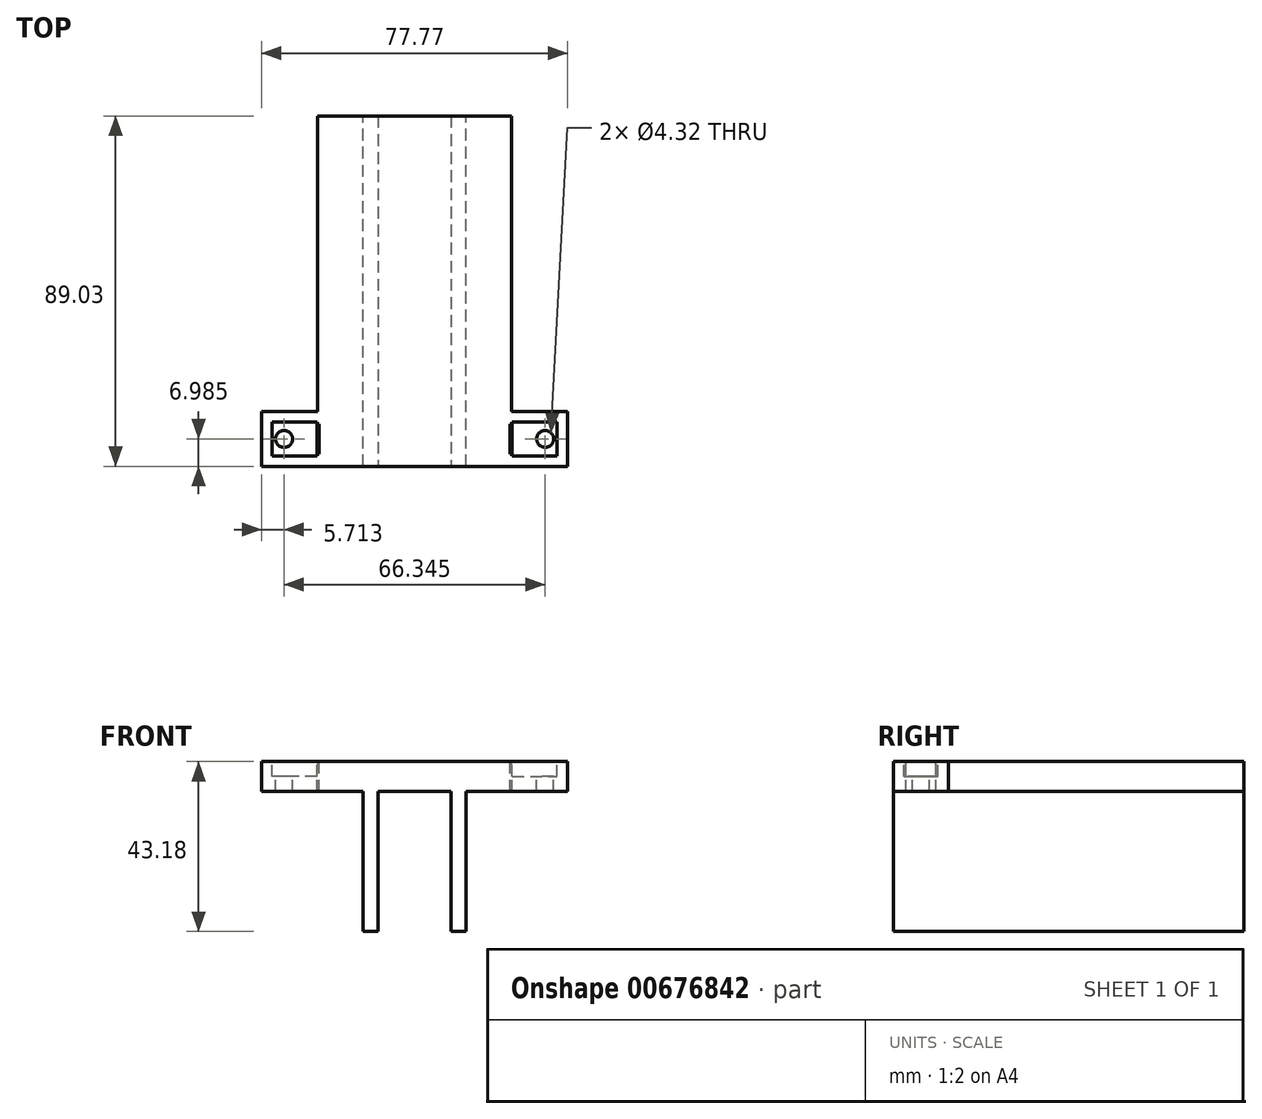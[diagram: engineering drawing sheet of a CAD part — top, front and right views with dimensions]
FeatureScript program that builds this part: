
annotation { "Feature Type Name" : "Feature", "Feature Type Description" : "" }
export const myFeature = defineFeature(function(context is Context, id is Id, definition is map)
    precondition{}
    {
        {
            var Q0;
            Q0=qCreatedBy(makeId("Top.planeOp"),FACE);
            var sketch = newSketch(context, id + "F0", { "sketchPlane" : qUnion([Q0])});
            skLineSegment(sketch, "E0.bottom", {"start": v(0, 0) * mm, "end": v(31.75, 0) * mm});
            skLineSegment(sketch, "E0.top", {"start": v(0, -63.5) * mm, "end": v(31.75, -63.5) * mm});
            skLineSegment(sketch, "E0.left", {"start": v(0, 0) * mm, "end": v(0, -63.5) * mm});
            skLineSegment(sketch, "E0.right", {"start": v(31.75, 0) * mm, "end": v(31.75, -63.5) * mm});
            skSolve(sketch);
        }
        {
            var Q0;
            Q0=qSketchRegion(id+"F0",true);
            extrude(context, id + "F1", {"entities" : qUnion([Q0]), "depth" : 7.62 * mm, "offsetDistance" : 25.4 * mm});
        }
        {
            var Q0;
            Q0=makeQuery(id+"F1.opExtrude","SWEPT_FACE",FACE,{"disambiguationData":[OSD([sQuery(id+"F0.wireOp",EDGE,"E0.top")])]});
            var sketch = newSketch(context, id + "F2", { "sketchPlane" : qUnion([Q0])});
            skLineSegment(sketch, "E1.bottom", {"start": v(21.74, 0) * mm, "end": v(10, 0) * mm});
            skLineSegment(sketch, "E1.top", {"start": v(21.74, 7.62) * mm, "end": v(10, 7.62) * mm});
            skLineSegment(sketch, "E1.left", {"start": v(21.74, 0) * mm, "end": v(21.74, 7.62) * mm});
            skLineSegment(sketch, "E1.right", {"start": v(10, 0) * mm, "end": v(10, 7.62) * mm});
            skSolve(sketch);
        }
        {
            var Q0;
            Q0=qSketchRegion(id+"F2",true);
            extrude(context, id + "F3", {"entities" : qUnion([Q0]), "operationType" : NewBodyOperationType.ADD, "depth" : 19.05 * mm, "offsetDistance" : 25.4 * mm});
        }
        {
            var Q0;
            Q0=makeQuery(id+"F3.opExtrude","SWEPT_FACE",FACE,{"disambiguationData":[OSD([sQuery(id+"F2.wireOp",EDGE,"E1.right")])]});
            var sketch = newSketch(context, id + "F4", { "sketchPlane" : qUnion([Q0])});
            skLineSegment(sketch, "E2.bottom", {"start": v(82.55, 7.62) * mm, "end": v(68.58, 7.62) * mm});
            skLineSegment(sketch, "E2.top", {"start": v(82.55, 0) * mm, "end": v(68.58, 0) * mm});
            skLineSegment(sketch, "E2.left", {"start": v(82.55, 7.62) * mm, "end": v(82.55, 0) * mm});
            skLineSegment(sketch, "E2.right", {"start": v(68.58, 7.62) * mm, "end": v(68.58, 0) * mm});
            skSolve(sketch);
        }
        {
            var Q0;
            Q0=makeQuery(id+"F4.imprint","IMPRINT",FACE,{"disambiguationData":[TD([[makeQuery(id+"F4.imprint","IMPRINT",EDGE,{"derivedFrom":sQuery(id+"F4.wireOp",EDGE,"E2.bottom")}),1.0]])]});
            extrude(context, id + "F5", {"entities" : qUnion([Q0]), "operationType" : NewBodyOperationType.ADD, "depth" : 33.02 * mm, "offsetDistance" : 25.4 * mm});
        }
        {
            var Q0;
            Q0=makeQuery(id+"F3.opExtrude","SWEPT_FACE",FACE,{"disambiguationData":[OSD([sQuery(id+"F2.wireOp",EDGE,"E1.left")])]});
            var sketch = newSketch(context, id + "F6", { "sketchPlane" : qUnion([Q0])});
            skLineSegment(sketch, "E3.bottom", {"start": v(-82.55, 0) * mm, "end": v(-68.58, 0) * mm});
            skLineSegment(sketch, "E3.top", {"start": v(-82.55, 7.62) * mm, "end": v(-68.58, 7.62) * mm});
            skLineSegment(sketch, "E3.left", {"start": v(-82.55, 0) * mm, "end": v(-82.55, 7.62) * mm});
            skLineSegment(sketch, "E3.right", {"start": v(-68.58, 0) * mm, "end": v(-68.58, 7.62) * mm});
            skSolve(sketch);
        }
        {
            var Q0;
            Q0=makeQuery(id+"F6.imprint","IMPRINT",FACE,{"disambiguationData":[TD([[makeQuery(id+"F6.imprint","IMPRINT",EDGE,{"derivedFrom":sQuery(id+"F6.wireOp",EDGE,"E3.bottom")}),1.0]])]});
            extrude(context, id + "F7", {"entities" : qUnion([Q0]), "operationType" : NewBodyOperationType.ADD, "depth" : 33.02 * mm, "offsetDistance" : 25.4 * mm});
        }
        {
            var Q0;
            Q0=makeQuery(id+"F7.boolean.opBoolean","MERGE",FACE,{"derivedFrom":[makeQuery(id+"F5.boolean.opBoolean","MERGE",FACE,{"derivedFrom":[makeQuery(id+"F3.boolean.opBoolean","MERGE",FACE,{"derivedFrom":[makeQuery(id+"F1.opExtrude","CAP_FACE",FACE,{"disambiguationData":[OSD([sQuery(id+"F0.wireOp",EDGE,"E0.bottom"),sQuery(id+"F0.wireOp",EDGE,"E0.top"),sQuery(id+"F0.wireOp",EDGE,"E0.left"),sQuery(id+"F0.wireOp",EDGE,"E0.right"),sQuery(id+"F0.wireOp",EDGE,"ZbQCodWJ-8rFa-9hVk-pMdy-9ETOQNlD702V"),sQuery(id+"F0.wireOp",EDGE,"mox7wiXO-owZT-BLzV-svZ2-wi7KJzRx0I65")])],"isStart":false}),makeQuery(id+"F3.opExtrude","SWEPT_FACE",FACE,{"disambiguationData":[OSD([sQuery(id+"F2.wireOp",EDGE,"E1.top")])]})]}),makeQuery(id+"F5.opExtrude","SWEPT_FACE",FACE,{"disambiguationData":[OSD([sQuery(id+"F4.wireOp",EDGE,"E2.bottom")])]})]}),makeQuery(id+"F7.opExtrude","SWEPT_FACE",FACE,{"disambiguationData":[OSD([sQuery(id+"F6.wireOp",EDGE,"E3.top")])]})]});
            var sketch = newSketch(context, id + "F8", { "sketchPlane" : qUnion([Q0])});
            skLineSegment(sketch, "E4.bottom", {"start": v(51.59, -71.75) * mm, "end": v(37.62, -71.75) * mm});
            skLineSegment(sketch, "E4.top", {"start": v(51.59, -79.37) * mm, "end": v(37.62, -79.37) * mm});
            skLineSegment(sketch, "E4.left", {"start": v(51.59, -71.75) * mm, "end": v(51.59, -79.37) * mm});
            skLineSegment(sketch, "E4.right", {"start": v(37.62, -71.75) * mm, "end": v(37.62, -79.37) * mm});
            skLineSegment(sketch, "E5.bottom", {"start": v(-5.87, -71.75) * mm, "end": v(-19.84, -71.75) * mm});
            skLineSegment(sketch, "E5.top", {"start": v(-5.87, -79.37) * mm, "end": v(-19.84, -79.37) * mm});
            skLineSegment(sketch, "E5.left", {"start": v(-5.87, -71.75) * mm, "end": v(-5.87, -79.37) * mm});
            skLineSegment(sketch, "E5.right", {"start": v(-19.84, -71.75) * mm, "end": v(-19.84, -79.37) * mm});
            skCircle(sketch, "E6", {"center": v(49.05, -75.56) * mm, "radius": 2.16 * mm});
            skCircle(sketch, "E7", {"center": v(-17.3, -75.56) * mm, "radius": 2.16 * mm});
            skLineSegment(sketch, "E8.bottom", {"start": v(37.62, -71.75) * mm, "end": v(40.16, -71.75) * mm});
            skLineSegment(sketch, "E8.top", {"start": v(37.62, -79.37) * mm, "end": v(40.16, -79.37) * mm});
            skLineSegment(sketch, "E8.right", {"start": v(40.16, -71.75) * mm, "end": v(40.16, -79.37) * mm});
            skLineSegment(sketch, "E9.bottom", {"start": v(-5.87, -71.75) * mm, "end": v(-8.4, -71.75) * mm});
            skLineSegment(sketch, "E9.top", {"start": v(-5.87, -79.37) * mm, "end": v(-8.4, -79.37) * mm});
            skLineSegment(sketch, "E9.right", {"start": v(-8.4, -71.75) * mm, "end": v(-8.4, -79.37) * mm});
            skLineSegment(sketch, "E10.bottom", {"start": v(40.67, -79.88) * mm, "end": v(37.1, -79.88) * mm});
            skLineSegment(sketch, "E10.top", {"start": v(40.67, -71.25) * mm, "end": v(37.1, -71.25) * mm});
            skLineSegment(sketch, "E10.left", {"start": v(40.67, -79.88) * mm, "end": v(40.67, -71.25) * mm});
            skLineSegment(sketch, "E10.right", {"start": v(37.1, -79.88) * mm, "end": v(37.1, -71.25) * mm});
            skLineSegment(sketch, "E11.bottom", {"start": v(-5.36, -79.88) * mm, "end": v(-8.92, -79.88) * mm});
            skLineSegment(sketch, "E11.top", {"start": v(-5.36, -71.25) * mm, "end": v(-8.92, -71.25) * mm});
            skLineSegment(sketch, "E11.left", {"start": v(-5.36, -79.88) * mm, "end": v(-5.36, -71.25) * mm});
            skLineSegment(sketch, "E11.right", {"start": v(-8.92, -79.88) * mm, "end": v(-8.92, -71.25) * mm});
            skLineSegment(sketch, "E12.left", {"start": v(40.67, -71.25) * mm, "end": v(40.67, -79.37) * mm});
            skLineSegment(sketch, "E13.bottom", {"start": v(40.67, -71.25) * mm, "end": v(52.1, -71.25) * mm});
            skLineSegment(sketch, "E13.top", {"start": v(40.67, -79.88) * mm, "end": v(52.1, -79.88) * mm});
            skLineSegment(sketch, "E13.left", {"start": v(40.67, -71.25) * mm, "end": v(40.67, -79.88) * mm});
            skLineSegment(sketch, "E13.right", {"start": v(52.1, -71.25) * mm, "end": v(52.1, -79.88) * mm});
            skLineSegment(sketch, "E14.bottom", {"start": v(-8.92, -71.25) * mm, "end": v(-20.35, -71.25) * mm});
            skLineSegment(sketch, "E14.top", {"start": v(-8.92, -79.88) * mm, "end": v(-20.35, -79.88) * mm});
            skLineSegment(sketch, "E14.left", {"start": v(-8.92, -71.25) * mm, "end": v(-8.92, -79.88) * mm});
            skLineSegment(sketch, "E14.right", {"start": v(-20.35, -71.25) * mm, "end": v(-20.35, -79.88) * mm});
            skSolve(sketch);
        }
        {
            var Q0;
            Q0=makeQuery(id+"F8.imprint","IMPRINT",FACE,{"disambiguationData":[TD([[makeQuery(id+"F8.imprint","IMPRINT",EDGE,{"derivedFrom":sQuery(id+"F8.wireOp",EDGE,"E6")}),1.0]])]});
            var Q1;
            {var subQ0=sQuery(id+"F8.wireOp",EDGE,"E8.bottom");Q1=makeQuery(id+"F8.imprint","IMPRINT",FACE,{"disambiguationData":[TD([[makeQuery(id+"F8.imprint","IMPRINT",EDGE,{"derivedFrom":subQ0}),1.0]])]});}
            var Q2;
            {var subQ0=sQuery(id+"F8.wireOp",EDGE,"E8.right");Q2=makeQuery(id+"F8.imprint","IMPRINT",FACE,{"disambiguationData":[TD([[makeQuery(id+"F8.imprint","IMPRINT",EDGE,{"derivedFrom":subQ0}),1.0]])]});}
            var Q3;
            Q3=makeQuery(id+"F8.imprint","IMPRINT",FACE,{"disambiguationData":[TD([[makeQuery(id+"F8.imprint","IMPRINT",EDGE,{"derivedFrom":sQuery(id+"F8.wireOp",EDGE,"E8.bottom")}),-1.0]])]});
            var Q4;
            Q4=makeQuery(id+"F8.imprint","IMPRINT",FACE,{"disambiguationData":[TD([[makeQuery(id+"F8.imprint","IMPRINT",EDGE,{"derivedFrom":sQuery(id+"F8.wireOp",EDGE,"E7")}),1.0]])]});
            var Q5;
            {var subQ0=sQuery(id+"F8.wireOp",EDGE,"E9.bottom");Q5=makeQuery(id+"F8.imprint","IMPRINT",FACE,{"disambiguationData":[TD([[makeQuery(id+"F8.imprint","IMPRINT",EDGE,{"derivedFrom":subQ0}),-1.0]])]});}
            var Q6;
            {var subQ0=sQuery(id+"F8.wireOp",EDGE,"E9.right");Q6=makeQuery(id+"F8.imprint","IMPRINT",FACE,{"disambiguationData":[TD([[makeQuery(id+"F8.imprint","IMPRINT",EDGE,{"derivedFrom":subQ0}),-1.0]])]});}
            var Q7;
            Q7=makeQuery(id+"F8.imprint","IMPRINT",FACE,{"disambiguationData":[TD([[makeQuery(id+"F8.imprint","IMPRINT",EDGE,{"derivedFrom":sQuery(id+"F8.wireOp",EDGE,"E9.bottom")}),1.0]])]});
            extrude(context, id + "F9", {"entities" : qUnion([Q0, Q1, Q2, Q3, Q4, Q5, Q6, Q7]), "operationType" : NewBodyOperationType.REMOVE, "endBound" : BoundingType.THROUGH_ALL, "oppositeDirection" : true, "depth" : 25.4 * mm, "offsetDistance" : 25.4 * mm});
        }
        {
            var Q0;
            Q0=makeQuery(id+"F3.opExtrude","SWEPT_FACE",FACE,{"disambiguationData":[OSD([sQuery(id+"F2.wireOp",EDGE,"E1.right")])]});
            extrude(context, id + "F10", {"entities" : qUnion([Q0]), "operationType" : NewBodyOperationType.ADD, "depth" : 10 * mm, "offsetDistance" : 25.4 * mm});
        }
        {
            var Q0;
            Q0=makeQuery(id+"F3.opExtrude","SWEPT_FACE",FACE,{"disambiguationData":[OSD([sQuery(id+"F2.wireOp",EDGE,"E1.left")])]});
            extrude(context, id + "F11", {"entities" : qUnion([Q0]), "operationType" : NewBodyOperationType.ADD, "depth" : 10 * mm, "offsetDistance" : 25.4 * mm});
        }
        {
            var Q0;
            {var subQ0=sQuery(id+"F8.wireOp",EDGE,"E4.left");Q0=makeQuery(id+"F8.imprint","IMPRINT",FACE,{"disambiguationData":[TD([[makeQuery(id+"F8.imprint","IMPRINT",EDGE,{"derivedFrom":subQ0}),-1.0]])]});}
            var Q1;
            {var subQ1=sQuery(id+"F8.wireOp",EDGE,"E4.left");Q1=makeQuery(id+"F8.imprint","IMPRINT",FACE,{"disambiguationData":[TD([[makeQuery(id+"F8.imprint","IMPRINT",EDGE,{"derivedFrom":subQ1}),1.0]])]});}
            var Q2;
            {var subQ0=sQuery(id+"F8.wireOp",EDGE,"E5.right");Q2=makeQuery(id+"F8.imprint","IMPRINT",FACE,{"disambiguationData":[TD([[makeQuery(id+"F8.imprint","IMPRINT",EDGE,{"derivedFrom":subQ0}),1.0]])]});}
            var Q3;
            {var subQ1=sQuery(id+"F8.wireOp",EDGE,"E5.right");Q3=makeQuery(id+"F8.imprint","IMPRINT",FACE,{"disambiguationData":[TD([[makeQuery(id+"F8.imprint","IMPRINT",EDGE,{"derivedFrom":subQ1}),-1.0]])]});}
            extrude(context, id + "F12", {"entities" : qUnion([Q0, Q1, Q2, Q3]), "operationType" : NewBodyOperationType.REMOVE, "oppositeDirection" : true, "depth" : 3.8 * mm, "offsetDistance" : 25.4 * mm});
        }
        {
            var Q0;
            Q0=makeQuery(id+"F10.boolean.opBoolean","MERGE",FACE,{"derivedFrom":[makeQuery(id+"F1.opExtrude","SWEPT_FACE",FACE,{"disambiguationData":[OSD([sQuery(id+"F0.wireOp",EDGE,"E0.left")])]}),makeQuery(id+"F10.opExtrude","CAP_FACE",FACE,{"disambiguationData":[OSD([sQuery(id+"F2.wireOp",EDGE,"E1.right")])],"isStart":false})]});
            extrude(context, id + "F13", {"entities" : qUnion([Q0]), "operationType" : NewBodyOperationType.ADD, "depth" : 8.75 * mm, "offsetDistance" : 25.4 * mm});
        }
        {
            var Q0;
            Q0=makeQuery(id+"F11.boolean.opBoolean","MERGE",FACE,{"derivedFrom":[makeQuery(id+"F1.opExtrude","SWEPT_FACE",FACE,{"disambiguationData":[OSD([sQuery(id+"F0.wireOp",EDGE,"E0.right")])]}),makeQuery(id+"F11.opExtrude","CAP_FACE",FACE,{"disambiguationData":[OSD([sQuery(id+"F2.wireOp",EDGE,"E1.left")])],"isStart":false})]});
            extrude(context, id + "F14", {"entities" : qUnion([Q0]), "operationType" : NewBodyOperationType.ADD, "depth" : 8.75 * mm, "offsetDistance" : 25.4 * mm});
        }
        {
            var Q0;
            {var subQ0=sQuery(id+"F0.wireOp",EDGE,"E0.bottom");Q0=makeQuery(id+"F14.boolean.opBoolean","MERGE",FACE,{"derivedFrom":[makeQuery(id+"F13.boolean.opBoolean","MERGE",FACE,{"derivedFrom":[makeQuery(id+"F1.opExtrude","SWEPT_FACE",FACE,{"disambiguationData":[OSD([subQ0])]}),makeQuery(id+"F13.opExtrude","SWEPT_FACE",FACE,{"disambiguationData":[OSD([subQ0,sQuery(id+"F0.wireOp",EDGE,"E0.left")])]})]}),makeQuery(id+"F14.opExtrude","SWEPT_FACE",FACE,{"disambiguationData":[OSD([subQ0,sQuery(id+"F0.wireOp",EDGE,"E0.right")])]})]});}
            extrude(context, id + "F15", {"entities" : qUnion([Q0]), "operationType" : NewBodyOperationType.ADD, "depth" : 6.48 * mm, "offsetDistance" : 25.4 * mm});
        }
        {
            var Q0;
            {var subQ0=sQuery(id+"F2.wireOp",EDGE,"E1.left");var subQ1=sQuery(id+"F2.wireOp",EDGE,"E1.bottom");var subQ2=sQuery(id+"F0.wireOp",EDGE,"E0.right");var subQ3=sQuery(id+"F0.wireOp",EDGE,"E0.top");var subQ4=sQuery(id+"F2.wireOp",EDGE,"E1.right");var subQ5=sQuery(id+"F0.wireOp",EDGE,"E0.left");Q0=makeQuery(id+"F14.boolean.opBoolean","MERGE",FACE,{"derivedFrom":[makeQuery(id+"F13.boolean.opBoolean","MERGE",FACE,{"derivedFrom":[makeQuery(id+"F11.boolean.opBoolean","MERGE",FACE,{"derivedFrom":[makeQuery(id+"F10.boolean.opBoolean","MERGE",FACE,{"derivedFrom":[makeQuery(id+"F7.boolean.opBoolean","MERGE",FACE,{"derivedFrom":[makeQuery(id+"F5.boolean.opBoolean","MERGE",FACE,{"derivedFrom":[makeQuery(id+"F3.boolean.opBoolean","MERGE",FACE,{"derivedFrom":[makeQuery(id+"F1.opExtrude","CAP_FACE",FACE,{"disambiguationData":[OSD([sQuery(id+"F0.wireOp",EDGE,"E0.bottom"),subQ3,subQ5,subQ2])],"isStart":true}),makeQuery(id+"F3.opExtrude","SWEPT_FACE",FACE,{"disambiguationData":[OSD([subQ1])]})]}),makeQuery(id+"F5.opExtrude","SWEPT_FACE",FACE,{"disambiguationData":[OSD([sQuery(id+"F4.wireOp",EDGE,"E2.top")])]})]}),makeQuery(id+"F7.opExtrude","SWEPT_FACE",FACE,{"disambiguationData":[OSD([sQuery(id+"F6.wireOp",EDGE,"E3.bottom")])]})]}),makeQuery(id+"F10.opExtrude","SWEPT_FACE",FACE,{"disambiguationData":[OSD([subQ3,subQ1,subQ4])]})]}),makeQuery(id+"F11.opExtrude","SWEPT_FACE",FACE,{"disambiguationData":[OSD([subQ3,subQ1,subQ0])]})]}),makeQuery(id+"F13.opExtrude","SWEPT_FACE",FACE,{"disambiguationData":[OSD([subQ3,subQ5,subQ1,subQ4])]})]}),makeQuery(id+"F14.opExtrude","SWEPT_FACE",FACE,{"disambiguationData":[OSD([subQ3,subQ2,subQ1,subQ0])]})]});}
            var sketch = newSketch(context, id + "F16", { "sketchPlane" : qUnion([Q0])});
            skLineSegment(sketch, "E15.bottom", {"start": v(25.13, -6.48) * mm, "end": v(6.62, -6.48) * mm});
            skLineSegment(sketch, "E15.top", {"start": v(25.13, 82.55) * mm, "end": v(6.62, 82.55) * mm});
            skLineSegment(sketch, "E15.left", {"start": v(25.13, -6.48) * mm, "end": v(25.13, 82.55) * mm});
            skLineSegment(sketch, "E15.right", {"start": v(6.62, -6.48) * mm, "end": v(6.62, 82.55) * mm});
            skLineSegment(sketch, "E16.bottom", {"start": v(6.62, -6.48) * mm, "end": v(25.13, -6.48) * mm});
            skLineSegment(sketch, "E16.top", {"start": v(6.62, -1.4) * mm, "end": v(25.13, -1.4) * mm});
            skLineSegment(sketch, "E16.left", {"start": v(6.62, -6.48) * mm, "end": v(6.62, -1.4) * mm});
            skLineSegment(sketch, "E16.right", {"start": v(25.13, -6.48) * mm, "end": v(25.13, -1.4) * mm});
            skLineSegment(sketch, "E17.bottom", {"start": v(6.62, 82.55) * mm, "end": v(25.13, 82.55) * mm});
            skLineSegment(sketch, "E17.top", {"start": v(6.62, 77.47) * mm, "end": v(25.13, 77.47) * mm});
            skLineSegment(sketch, "E17.left", {"start": v(6.62, 82.55) * mm, "end": v(6.62, 77.47) * mm});
            skLineSegment(sketch, "E17.right", {"start": v(25.13, 82.55) * mm, "end": v(25.13, 77.47) * mm});
            skLineSegment(sketch, "E18.bottom", {"start": v(6.62, 82.55) * mm, "end": v(2.8, 82.55) * mm});
            skLineSegment(sketch, "E18.top", {"start": v(6.62, -6.48) * mm, "end": v(2.8, -6.48) * mm});
            skLineSegment(sketch, "E18.left", {"start": v(6.62, 82.55) * mm, "end": v(6.62, -6.48) * mm});
            skLineSegment(sketch, "E18.right", {"start": v(2.8, 82.55) * mm, "end": v(2.8, -6.48) * mm});
            skLineSegment(sketch, "E19.bottom", {"start": v(25.13, 82.55) * mm, "end": v(28.94, 82.55) * mm});
            skLineSegment(sketch, "E19.top", {"start": v(25.13, -6.48) * mm, "end": v(28.94, -6.48) * mm});
            skLineSegment(sketch, "E19.left", {"start": v(25.13, 82.55) * mm, "end": v(25.13, -6.48) * mm});
            skLineSegment(sketch, "E19.right", {"start": v(28.94, 82.55) * mm, "end": v(28.94, -6.48) * mm});
            skLineSegment(sketch, "E20.bottom", {"start": v(-8.75, 68.58) * mm, "end": v(-6.08, 68.58) * mm});
            skLineSegment(sketch, "E20.top", {"start": v(-8.75, -6.48) * mm, "end": v(-6.08, -6.48) * mm});
            skLineSegment(sketch, "E20.left", {"start": v(-8.75, 68.58) * mm, "end": v(-8.75, -6.48) * mm});
            skLineSegment(sketch, "E20.right", {"start": v(-6.08, 68.58) * mm, "end": v(-6.08, -6.48) * mm});
            skLineSegment(sketch, "E21.bottom", {"start": v(40.5, 68.58) * mm, "end": v(37.83, 68.58) * mm});
            skLineSegment(sketch, "E21.top", {"start": v(40.5, -6.48) * mm, "end": v(37.83, -6.48) * mm});
            skLineSegment(sketch, "E21.left", {"start": v(40.5, 68.58) * mm, "end": v(40.5, -6.48) * mm});
            skLineSegment(sketch, "E21.right", {"start": v(37.83, 68.58) * mm, "end": v(37.83, -6.48) * mm});
            skSolve(sketch);
        }
        {
            var Q0;
            {var subQ0=sQuery(id+"F16.wireOp",EDGE,"E16.bottom");Q0=makeQuery(id+"F16.imprint","IMPRINT",FACE,{"disambiguationData":[TD([[makeQuery(id+"F16.imprint","IMPRINT",EDGE,{"derivedFrom":subQ0}),1.0]])]});}
            var Q1;
            {var subQ0=sQuery(id+"F16.wireOp",EDGE,"E17.bottom");Q1=makeQuery(id+"F16.imprint","IMPRINT",FACE,{"disambiguationData":[TD([[makeQuery(id+"F16.imprint","IMPRINT",EDGE,{"derivedFrom":subQ0}),-1.0]])]});}
            var Q2;
            {var subQ3=sQuery(id+"F16.wireOp",EDGE,"E18.bottom");Q2=makeQuery(id+"F16.imprint","IMPRINT",FACE,{"disambiguationData":[TD([[makeQuery(id+"F16.imprint","IMPRINT",EDGE,{"derivedFrom":subQ3}),-1.0]])]});}
            var Q3;
            {var subQ3=sQuery(id+"F16.wireOp",EDGE,"E19.bottom");Q3=makeQuery(id+"F16.imprint","IMPRINT",FACE,{"disambiguationData":[TD([[makeQuery(id+"F16.imprint","IMPRINT",EDGE,{"derivedFrom":subQ3}),-1.0]])]});}
            extrude(context, id + "F17", {"entities" : qUnion([Q0, Q1, Q2, Q3]), "operationType" : NewBodyOperationType.ADD, "depth" : 35.56 * mm, "offsetDistance" : 25.4 * mm});
        }
    });
